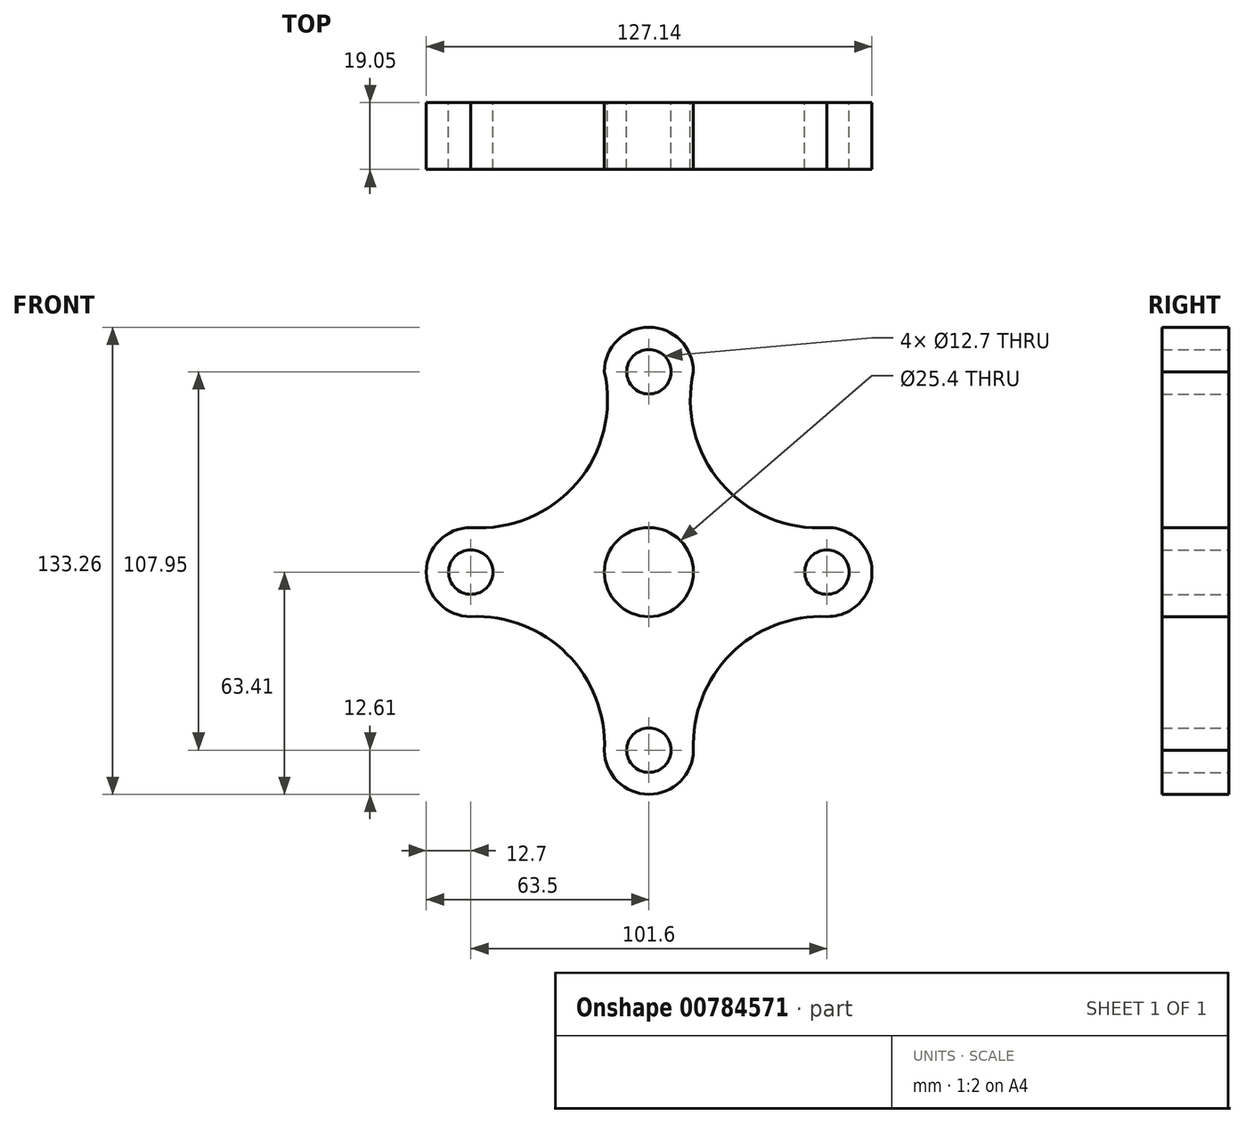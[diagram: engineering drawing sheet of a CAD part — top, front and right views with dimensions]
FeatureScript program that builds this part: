
annotation { "Feature Type Name" : "Feature", "Feature Type Description" : "" }
export const myFeature = defineFeature(function(context is Context, id is Id, definition is map)
    precondition{}
    {
        {
            var Q0;
            Q0=qCreatedBy(makeId("Front.planeOp"),FACE);
            var sketch = newSketch(context, id + "F0", { "sketchPlane" : qUnion([Q0])});
            skCircle(sketch, "E0", {"center": v(0, 0) * mm, "radius": 12.7 * mm});
            skCircle(sketch, "E1", {"center": v(0, 57.15) * mm, "radius": 6.35 * mm});
            skCircle(sketch, "E2", {"center": v(50.8, 0) * mm, "radius": 6.35 * mm});
            skCircle(sketch, "E3", {"center": v(-50.8, 0) * mm, "radius": 6.35 * mm});
            skCircle(sketch, "E4", {"center": v(0, -50.8) * mm, "radius": 6.35 * mm});
            skArc(sketch, "E5", {"start": v(-12.7, -50.8) * mm, "mid": v(-23.36, -23.36) * mm, "end": v(-50.8, -12.7) * mm});
            skArc(sketch, "E6", {"start": v(50.8, -12.7) * mm, "mid": v(23.36, -23.36) * mm, "end": v(12.7, -50.8) * mm});
            skArc(sketch, "E7", {"start": v(12.7, 57.15) * mm, "mid": v(20.6, 25.37) * mm, "end": v(50.8, 12.7) * mm});
            skArc(sketch, "E8", {"start": v(-50.8, 12.7) * mm, "mid": v(-20.6, 25.37) * mm, "end": v(-12.7, 57.15) * mm});
            skArc(sketch, "E9", {"start": v(-50.8, 12.7) * mm, "mid": v(-63.5, 0) * mm, "end": v(-50.8, -12.7) * mm});
            skArc(sketch, "E10", {"start": v(-12.7, -50.8) * mm, "mid": v(0, -63.41) * mm, "end": v(12.7, -50.8) * mm});
            skArc(sketch, "E11", {"start": v(50.8, -12.7) * mm, "mid": v(63.64, 0) * mm, "end": v(50.8, 12.7) * mm});
            skArc(sketch, "E12", {"start": v(12.7, 57.15) * mm, "mid": v(0, 69.85) * mm, "end": v(-12.7, 57.15) * mm});
            skLineSegment(sketch, "E13.trimOffspring", {"start": v(0, -50.71) * mm, "end": v(0, -50.8) * mm});
            skSolve(sketch);
        }
        {
            var Q0;
            Q0=makeQuery(id+"F0.imprint","IMPRINT",FACE,{"disambiguationData":[TD([[makeQuery(id+"F0.imprint","IMPRINT",EDGE,{"derivedFrom":sQuery(id+"F0.wireOp",EDGE,"E0")}),-1.0]])]});
            extrude(context, id + "F1", {"entities" : qUnion([Q0]), "depth" : 19.05 * mm, "offsetDistance" : 25.4 * mm});
        }
    });
